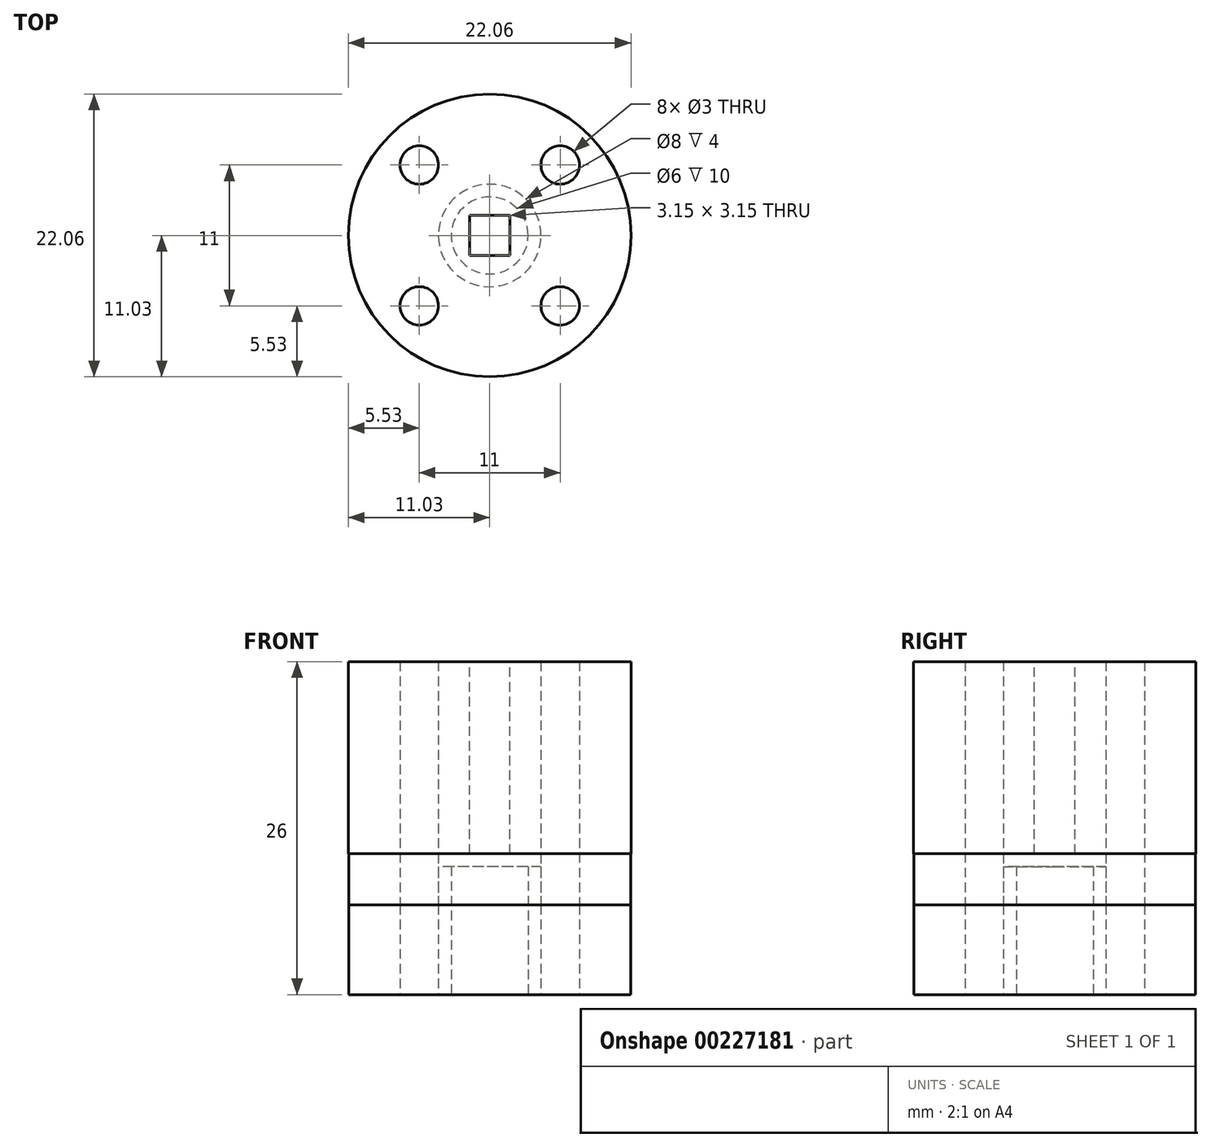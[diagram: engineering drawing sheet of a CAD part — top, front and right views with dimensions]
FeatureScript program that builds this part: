
annotation { "Feature Type Name" : "Feature", "Feature Type Description" : "" }
export const myFeature = defineFeature(function(context is Context, id is Id, definition is map)
    precondition{}
    {
        {
            var Q0;
            Q0=qCreatedBy(makeId("Top.planeOp"),FACE);
            var sketch = newSketch(context, id + "F0", { "sketchPlane" : qUnion([Q0])});
            skCircle(sketch, "E0", {"center": v(0, 0) * mm, "radius": 11 * mm});
            skCircle(sketch, "E1", {"center": v(0, 0) * mm, "radius": 3 * mm});
            skCircle(sketch, "E2", {"center": v(0, 0) * mm, "radius": 4 * mm});
            skLineSegment(sketch, "E3.bottom", {"start": v(5.5, 5.5) * mm, "end": v(-5.5, 5.5) * mm, "construction": true});
            skLineSegment(sketch, "E3.top", {"start": v(5.5, -5.5) * mm, "end": v(-5.5, -5.5) * mm, "construction": true});
            skLineSegment(sketch, "E3.left", {"start": v(5.5, 5.5) * mm, "end": v(5.5, -5.5) * mm, "construction": true});
            skLineSegment(sketch, "E3.right", {"start": v(-5.5, 5.5) * mm, "end": v(-5.5, -5.5) * mm, "construction": true});
            skCircle(sketch, "E4", {"center": v(-5.5, 5.5) * mm, "radius": 1.5 * mm});
            skCircle(sketch, "E5.1.0", {"center": v(-5.5, -5.5) * mm, "radius": 1.5 * mm});
            skCircle(sketch, "E5.2.0", {"center": v(5.5, -5.5) * mm, "radius": 1.5 * mm});
            skCircle(sketch, "E5.3.0", {"center": v(5.5, 5.5) * mm, "radius": 1.5 * mm});
            skSolve(sketch);
        }
        {
            var Q0;
            Q0=makeQuery(id+"F0.imprint","IMPRINT",FACE,{"disambiguationData":[TD([[makeQuery(id+"F0.imprint","IMPRINT",EDGE,{"derivedFrom":sQuery(id+"F0.wireOp",EDGE,"E0")}),1.0]])]});
            extrude(context, id + "F1", {"entities" : qUnion([Q0]), "depth" : 7 * mm});
        }
        {
            var Q0;
            Q0=makeQuery(id+"F0.imprint","IMPRINT",FACE,{"disambiguationData":[TD([[makeQuery(id+"F0.imprint","IMPRINT",EDGE,{"derivedFrom":sQuery(id+"F0.wireOp",EDGE,"E1")}),-1.0]])]});
            extrude(context, id + "F2", {"entities" : qUnion([Q0]), "operationType" : NewBodyOperationType.ADD, "depth" : 10 * mm});
        }
        {
            var Q0;
            Q0=makeQuery(id+"F1.opExtrude","CAP_FACE",FACE,{"disambiguationData":[OSD([sQuery(id+"F0.wireOp",EDGE,"E0"),sQuery(id+"F0.wireOp",EDGE,"E2"),sQuery(id+"F0.wireOp",EDGE,"E4"),sQuery(id+"F0.wireOp",EDGE,"E5.1.0"),sQuery(id+"F0.wireOp",EDGE,"E5.2.0"),sQuery(id+"F0.wireOp",EDGE,"E5.3.0")])],"isStart":false});
            var sketch = newSketch(context, id + "F3", { "sketchPlane" : qUnion([Q0])});
            skCircle(sketch, "E6", {"center": v(0, 0) * mm, "radius": 11 * mm});
            skCircle(sketch, "E7", {"center": v(5.5, 5.5) * mm, "radius": 1.5 * mm});
            skCircle(sketch, "E8.1.0", {"center": v(-5.5, 5.5) * mm, "radius": 1.5 * mm});
            skCircle(sketch, "E8.2.0", {"center": v(-5.5, -5.5) * mm, "radius": 1.5 * mm});
            skCircle(sketch, "E8.3.0", {"center": v(5.5, -5.5) * mm, "radius": 1.5 * mm});
            skSolve(sketch);
        }
        {
            var Q0;
            Q0=makeQuery(id+"F3.imprint","IMPRINT",FACE,{"disambiguationData":[TD([[makeQuery(id+"F3.imprint","IMPRINT",EDGE,{"derivedFrom":sQuery(id+"F3.wireOp",EDGE,"E6")}),1.0]])]});
            extrude(context, id + "F4", {"entities" : qUnion([Q0]), "depth" : 4 * mm});
        }
        {
            var Q0;
            Q0=makeQuery(id+"F4.opExtrude","CAP_FACE",FACE,{"disambiguationData":[OSD([sQuery(id+"F0.wireOp",EDGE,"E2"),sQuery(id+"F3.wireOp",EDGE,"E6"),sQuery(id+"F3.wireOp",EDGE,"E7"),sQuery(id+"F3.wireOp",EDGE,"E8.1.0"),sQuery(id+"F3.wireOp",EDGE,"E8.2.0"),sQuery(id+"F3.wireOp",EDGE,"E8.3.0")])],"isStart":false});
            var sketch = newSketch(context, id + "F5", { "sketchPlane" : qUnion([Q0])});
            skCircle(sketch, "E9", {"center": v(0, 0) * mm, "radius": 11.03 * mm});
            skSolve(sketch);
        }
        {
            var Q0;
            Q0 = qSketchRegion(id + "F5", true);
            extrude(context, id + "F6", {"entities" : qUnion([Q0]), "operationType" : NewBodyOperationType.ADD, "depth" : 15 * mm});
        }
        {
            var Q0;
            Q0=makeQuery(id+"F6.opExtrude","CAP_FACE",FACE,{"disambiguationData":[OSD([sQuery(id+"F5.wireOp",EDGE,"E9")])],"isStart":false});
            var sketch = newSketch(context, id + "F7", { "sketchPlane" : qUnion([Q0])});
            skLineSegment(sketch, "E10.bottom", {"start": v(1.57, 1.57) * mm, "end": v(-1.57, 1.58) * mm});
            skLineSegment(sketch, "E10.top", {"start": v(1.57, -1.57) * mm, "end": v(-1.58, -1.57) * mm});
            skLineSegment(sketch, "E10.left", {"start": v(1.57, 1.57) * mm, "end": v(1.57, -1.58) * mm});
            skLineSegment(sketch, "E10.right", {"start": v(-1.57, 1.58) * mm, "end": v(-1.57, -1.57) * mm});
            skPoint(sketch, "E10.middle", {"position": v(0, 0) * mm});
            skSolve(sketch);
        }
        {
            var Q0;
            Q0=makeQuery(id+"F7.imprint","IMPRINT",FACE,{"disambiguationData":[TD([[makeQuery(id+"F7.imprint","IMPRINT",EDGE,{"derivedFrom":sQuery(id+"F7.wireOp",EDGE,"E10.bottom")}),1.0]])]});
            extrude(context, id + "F8", {"entities" : qUnion([Q0]), "operationType" : NewBodyOperationType.REMOVE, "oppositeDirection" : true, "depth" : 16.3 * mm});
        }
        {
            var Q0;
            Q0=makeQuery(id+"F5.imprint","IMPRINT",FACE,{"disambiguationData":[TD([[makeQuery(id+"F5.imprint","IMPRINT",EDGE,{"derivedFrom":makeQuery(id+"F4.opExtrude","CAP_EDGE",EDGE,{"disambiguationData":[OSD([sQuery(id+"F3.wireOp",EDGE,"E8.1.0")])],"isStart":false})}),1.0]])]});
            var Q1;
            Q1=makeQuery(id+"F5.imprint","IMPRINT",FACE,{"disambiguationData":[TD([[makeQuery(id+"F5.imprint","IMPRINT",EDGE,{"derivedFrom":makeQuery(id+"F4.opExtrude","CAP_EDGE",EDGE,{"disambiguationData":[OSD([sQuery(id+"F3.wireOp",EDGE,"E7")])],"isStart":false})}),1.0]])]});
            var Q2;
            Q2=makeQuery(id+"F5.imprint","IMPRINT",FACE,{"disambiguationData":[TD([[makeQuery(id+"F5.imprint","IMPRINT",EDGE,{"derivedFrom":makeQuery(id+"F4.opExtrude","CAP_EDGE",EDGE,{"disambiguationData":[OSD([sQuery(id+"F3.wireOp",EDGE,"E8.3.0")])],"isStart":false})}),1.0]])]});
            var Q3;
            Q3=makeQuery(id+"F5.imprint","IMPRINT",FACE,{"disambiguationData":[TD([[makeQuery(id+"F5.imprint","IMPRINT",EDGE,{"derivedFrom":makeQuery(id+"F4.opExtrude","CAP_EDGE",EDGE,{"disambiguationData":[OSD([sQuery(id+"F3.wireOp",EDGE,"E8.2.0")])],"isStart":false})}),1.0]])]});
            extrude(context, id + "F9", {"entities" : qUnion([Q0, Q1, Q2, Q3]), "operationType" : NewBodyOperationType.REMOVE, "depth" : 46.4 * mm});
        }
    });
